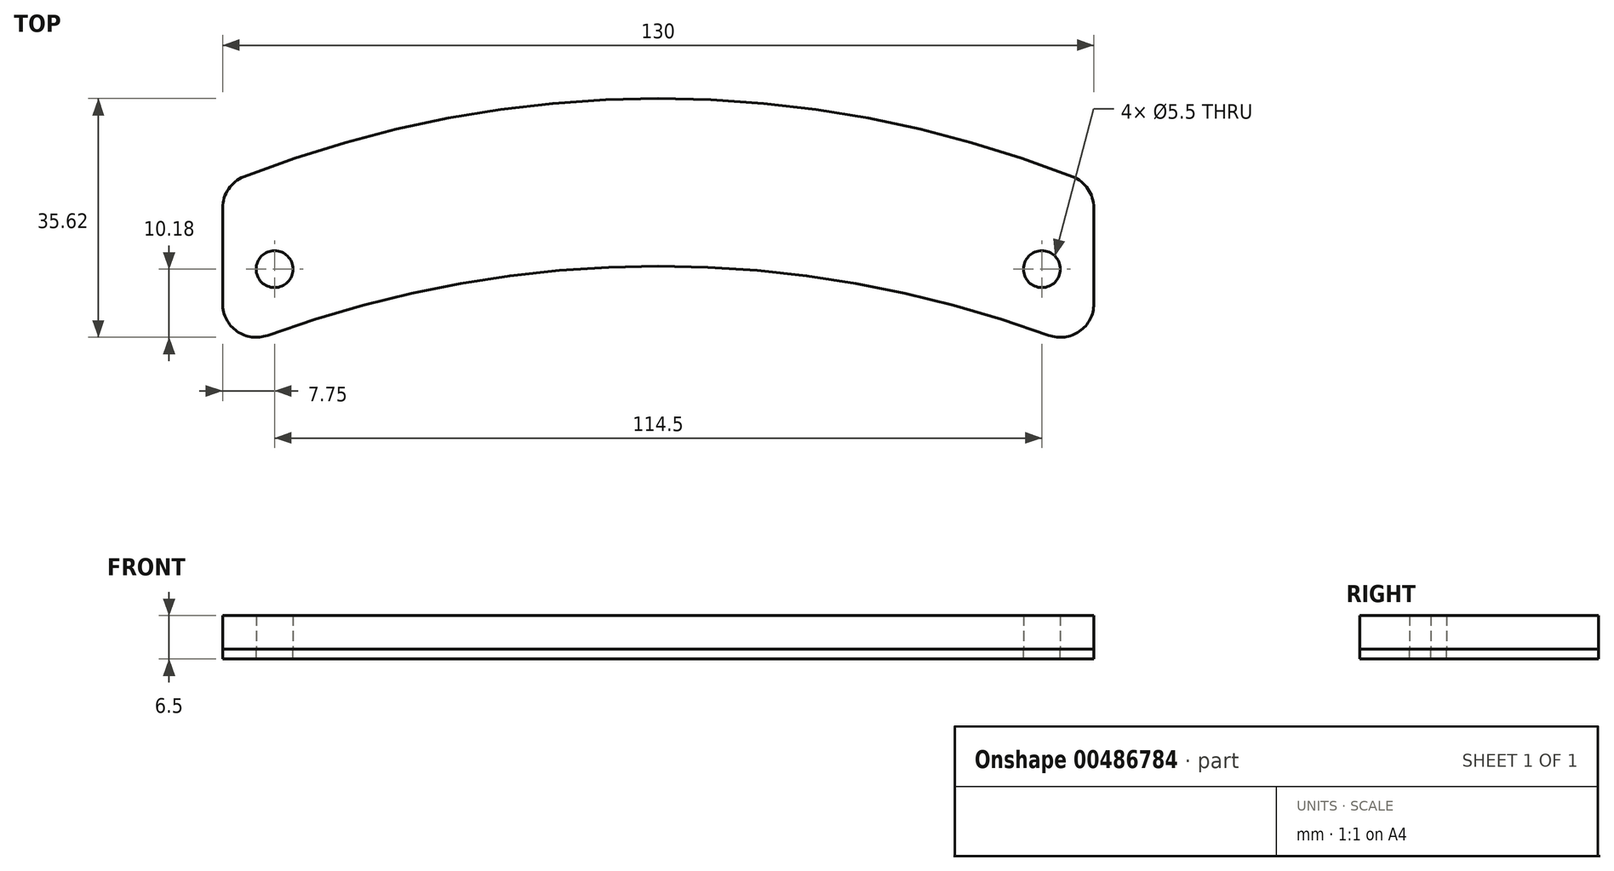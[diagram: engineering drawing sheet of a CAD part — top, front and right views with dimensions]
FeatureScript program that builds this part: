
annotation { "Feature Type Name" : "Feature", "Feature Type Description" : "" }
export const myFeature = defineFeature(function(context is Context, id is Id, definition is map)
    precondition{}
    {
        {
            var Q0;
            Q0=qCreatedBy(makeId("Top.planeOp"),FACE);
            var sketch = newSketch(context, id + "F0", { "sketchPlane" : qUnion([Q0])});
            skLineSegment(sketch, "E0.left", {"start": v(65, -12.5) * mm, "end": v(65, 12.5) * mm});
            skLineSegment(sketch, "E0.right", {"start": v(-65, -12.5) * mm, "end": v(-65, 12.5) * mm});
            skPoint(sketch, "E0.middle", {"position": v(0, 0) * mm});
            skArc(sketch, "E1", {"start": v(65, -12.5) * mm, "mid": v(0, 0.44) * mm, "end": v(-65, -12.5) * mm});
            skArc(sketch, "E2", {"start": v(65, 12.5) * mm, "mid": v(0, 25.44) * mm, "end": v(-65, 12.5) * mm});
            skCircle(sketch, "E3", {"center": v(57.25, 0) * mm, "radius": 2.75 * mm});
            skLineSegment(sketch, "E4", {"start": v(65, 5.5) * mm, "end": v(57.25, 5.5) * mm, "construction": true});
            skLineSegment(sketch, "E5", {"start": v(65, -5.5) * mm, "end": v(57.25, -5.5) * mm, "construction": true});
            skArc(sketch, "E6", {"start": v(57.25, 5.5) * mm, "mid": v(51.75, 0) * mm, "end": v(57.25, -5.5) * mm, "construction": true});
            skLineSegment(sketch, "E7", {"start": v(0, 25.44) * mm, "end": v(0, -15.83) * mm, "construction": true});
            skLineSegment(sketch, "E8.MirrorCS", {"start": v(-65, 5.5) * mm, "end": v(-57.25, 5.5) * mm, "construction": true});
            skArc(sketch, "E9.MirrorCS", {"start": v(-57.25, 5.5) * mm, "mid": v(-51.75, 0) * mm, "end": v(-57.25, -5.5) * mm, "construction": true});
            skLineSegment(sketch, "E10.MirrorCS", {"start": v(-65, -5.5) * mm, "end": v(-57.25, -5.5) * mm, "construction": true});
            skCircle(sketch, "E11.MirrorC", {"center": v(-57.25, 0) * mm, "radius": 2.75 * mm});
            skSolve(sketch);
        }
        {
            var Q0;
            Q0=makeQuery(id+"F0.imprint","IMPRINT",FACE,{"disambiguationData":[TD([[makeQuery(id+"F0.imprint","IMPRINT",EDGE,{"derivedFrom":sQuery(id+"F0.wireOp",EDGE,"E0.left")}),1.0]])]});
            extrude(context, id + "F1", {"entities" : qUnion([Q0]), "depth" : 5 * mm, "offsetDistance" : 25 * mm});
        }
        {
            var Q0;
            Q0=makeQuery(id+"F0.imprint","IMPRINT",FACE,{"disambiguationData":[TD([[makeQuery(id+"F0.imprint","IMPRINT",EDGE,{"derivedFrom":sQuery(id+"F0.wireOp",EDGE,"E0.left")}),1.0]])]});
            extrude(context, id + "F2", {"entities" : qUnion([Q0]), "oppositeDirection" : true, "depth" : 1.5 * mm, "offsetDistance" : 25 * mm});
        }
        {
            var Q0;
            Q0=makeQuery(id+"F1.opExtrude","SWEPT_EDGE",EDGE,{"disambiguationData":[OSD([sQuery(id+"F0.wireOp",EDGE,"E0.right"),sQuery(id+"F0.wireOp",EDGE,"E1")])]});
            var Q1;
            Q1=makeQuery(id+"F2.opExtrude","SWEPT_EDGE",EDGE,{"disambiguationData":[OSD([sQuery(id+"F0.wireOp",EDGE,"E0.right"),sQuery(id+"F0.wireOp",EDGE,"E1")])]});
            var Q2;
            Q2=makeQuery(id+"F2.opExtrude","SWEPT_EDGE",EDGE,{"disambiguationData":[OSD([sQuery(id+"F0.wireOp",EDGE,"E0.left"),sQuery(id+"F0.wireOp",EDGE,"E1")])]});
            var Q3;
            Q3=makeQuery(id+"F1.opExtrude","SWEPT_EDGE",EDGE,{"disambiguationData":[OSD([sQuery(id+"F0.wireOp",EDGE,"E0.left"),sQuery(id+"F0.wireOp",EDGE,"E1")])]});
            var Q4;
            Q4=makeQuery(id+"F2.opExtrude","SWEPT_EDGE",EDGE,{"disambiguationData":[OSD([sQuery(id+"F0.wireOp",EDGE,"E0.left"),sQuery(id+"F0.wireOp",EDGE,"E2")])]});
            var Q5;
            Q5=makeQuery(id+"F1.opExtrude","SWEPT_EDGE",EDGE,{"disambiguationData":[OSD([sQuery(id+"F0.wireOp",EDGE,"E0.left"),sQuery(id+"F0.wireOp",EDGE,"E2")])]});
            var Q6;
            Q6=makeQuery(id+"F2.opExtrude","SWEPT_EDGE",EDGE,{"disambiguationData":[OSD([sQuery(id+"F0.wireOp",EDGE,"E0.right"),sQuery(id+"F0.wireOp",EDGE,"E2")])]});
            var Q7;
            Q7=makeQuery(id+"F1.opExtrude","SWEPT_EDGE",EDGE,{"disambiguationData":[OSD([sQuery(id+"F0.wireOp",EDGE,"E0.right"),sQuery(id+"F0.wireOp",EDGE,"E2")])]});
            fillet(context, id + "F3", {"entities" : qUnion([Q0, Q1, Q2, Q3, Q4, Q5, Q6, Q7]), "radius" : 5 * mm, "tangentPropagation" : true, "allowEdgeOverflow" : false});
        }
    });
